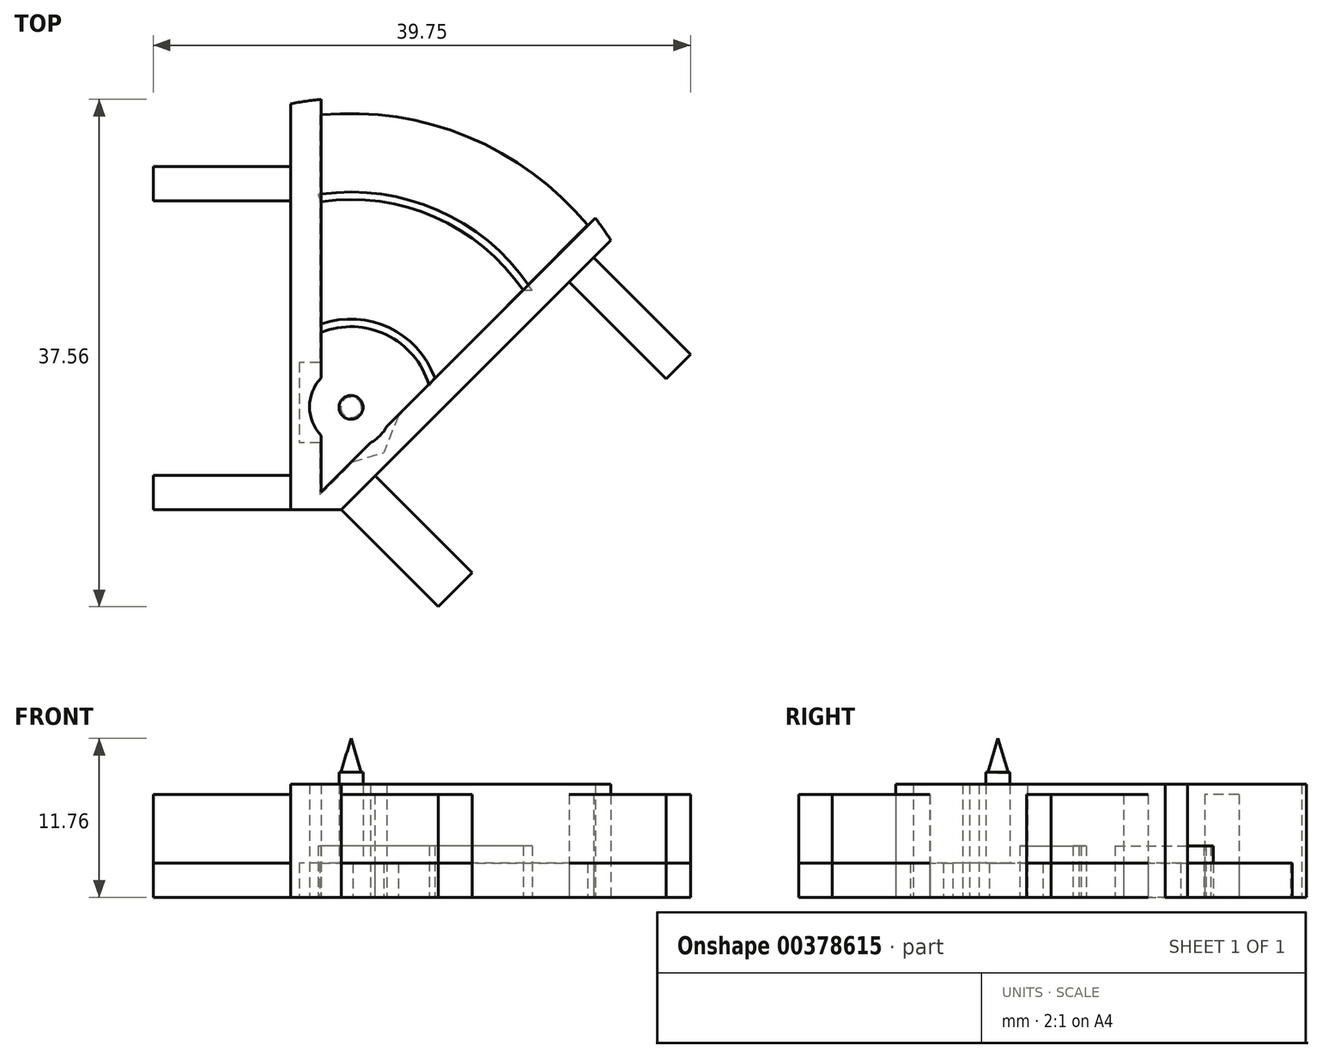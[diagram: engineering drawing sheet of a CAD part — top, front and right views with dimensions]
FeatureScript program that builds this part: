
annotation { "Feature Type Name" : "Feature", "Feature Type Description" : "" }
export const myFeature = defineFeature(function(context is Context, id is Id, definition is map)
    precondition{}
    {
        {
            var Q0;
            Q0=qCreatedBy(makeId("Top.planeOp"),FACE);
            var sketch = newSketch(context, id + "F0", { "sketchPlane" : qUnion([Q0])});
            skCircle(sketch, "E0", {"center": v(0, 0) * mm, "radius": 35.56 * mm});
            skLineSegment(sketch, "E1", {"start": v(0, 0) * mm, "end": v(0, 35.56) * mm});
            skLineSegment(sketch, "E2", {"start": v(0, 0) * mm, "end": v(35.56, 0) * mm});
            skPoint(sketch, "E3", {"position": v(4.45, 7.62) * mm});
            skCircle(sketch, "E4", {"center": v(4.45, 7.62) * mm, "radius": 1.27 * mm});
            skLineSegment(sketch, "E5", {"start": v(2.28, 35.49) * mm, "end": v(2.28, 0) * mm});
            skArc(sketch, "E6", {"start": v(26, 0) * mm, "mid": v(21.73, 22.58) * mm, "end": v(0, 30.04) * mm});
            skLineSegment(sketch, "E7", {"start": v(2.28, 1.31) * mm, "end": v(25.62, 24.66) * mm});
            skLineSegment(sketch, "E8", {"start": v(2.28, -1.47) * mm, "end": v(26.95, 23.2) * mm});
            skArc(sketch, "E9", {"start": v(29.85, 0) * mm, "mid": v(24.32, 25.19) * mm, "end": v(0, 33.77) * mm});
            skCircle(sketch, "E10", {"center": v(4.45, 7.62) * mm, "radius": 3.05 * mm});
            skSolve(sketch);
        }
        {
            var Q0;
            {var subQ0=sQuery(id+"F0.wireOp",EDGE,"E7");var subQ1=sQuery(id+"F0.wireOp",EDGE,"E5");var subQ2=makeQuery(id+"F0.imprint","INTERSECT",VERTEX,{"derivedFrom":[subQ1,subQ0]});Q0=makeQuery(id+"F0.imprint","IMPRINT",FACE,{"disambiguationData":[TD([[makeQuery(id+"F0.imprint","IMPRINT",EDGE,{"disambiguationData":[TD([[subQ2,-1.0]])],"derivedFrom":subQ1}),1.0]])]});}
            var Q1;
            {var subQ5=sQuery(id+"F0.wireOp",EDGE,"E2");var subQ6=sQuery(id+"F0.wireOp",EDGE,"E1");var subQ7=makeQuery(id+"F0.imprint","INTERSECT",VERTEX,{"derivedFrom":[subQ6,subQ5]});Q1=makeQuery(id+"F0.imprint","IMPRINT",FACE,{"disambiguationData":[TD([[makeQuery(id+"F0.imprint","IMPRINT",EDGE,{"disambiguationData":[TD([[subQ7,-1.0]])],"derivedFrom":subQ6}),-1.0]])]});}
            extrude(context, id + "F1", {"entities" : qUnion([Q0, Q1]), "depth" : 8.38 * mm});
        }
        {
            var Q0;
            Q0=qCreatedBy(makeId("Top.planeOp"),FACE);
            var sketch = newSketch(context, id + "F2", { "sketchPlane" : qUnion([Q0])});
            skLineSegment(sketch, "E11", {"start": v(0, 0) * mm, "end": v(3.74, 0) * mm});
            skLineSegment(sketch, "E12", {"start": v(3.74, 0) * mm, "end": v(25.98, 22.24) * mm});
            skLineSegment(sketch, "E13", {"start": v(0, 30.67) * mm, "end": v(0, 0) * mm});
            skLineSegment(sketch, "E14.bottom", {"start": v(0, 2.54) * mm, "end": v(-10.16, 2.54) * mm});
            skLineSegment(sketch, "E14.top", {"start": v(0, 0) * mm, "end": v(-10.16, 0) * mm});
            skLineSegment(sketch, "E14.left", {"start": v(0, 2.54) * mm, "end": v(0, 0) * mm});
            skLineSegment(sketch, "E14.right", {"start": v(-10.16, 2.54) * mm, "end": v(-10.16, 0) * mm});
            skLineSegment(sketch, "E15.bottom", {"start": v(0, 25.4) * mm, "end": v(-10.16, 25.4) * mm});
            skLineSegment(sketch, "E15.top", {"start": v(0, 22.86) * mm, "end": v(-10.16, 22.86) * mm});
            skLineSegment(sketch, "E15.left", {"start": v(0, 25.4) * mm, "end": v(0, 22.86) * mm});
            skLineSegment(sketch, "E15.right", {"start": v(-10.16, 25.4) * mm, "end": v(-10.16, 22.86) * mm});
            skLineSegment(sketch, "E16", {"start": v(3.74, 0) * mm, "end": v(10.93, -7.18) * mm});
            skLineSegment(sketch, "E17", {"start": v(10.93, -7.18) * mm, "end": v(13.43, -4.68) * mm});
            skLineSegment(sketch, "E18", {"start": v(13.43, -4.68) * mm, "end": v(6.24, 2.5) * mm});
            skLineSegment(sketch, "E19", {"start": v(20.61, 16.87) * mm, "end": v(27.8, 9.69) * mm});
            skLineSegment(sketch, "E20", {"start": v(27.8, 9.69) * mm, "end": v(29.6, 11.48) * mm});
            skLineSegment(sketch, "E21", {"start": v(29.6, 11.48) * mm, "end": v(22.4, 18.67) * mm});
            skLineSegment(sketch, "E22", {"start": v(22.4, 18.67) * mm, "end": v(20.61, 16.87) * mm});
            skLineSegment(sketch, "E23", {"start": v(6.24, 2.5) * mm, "end": v(3.74, 0) * mm});
            skLineSegment(sketch, "E24.bottom", {"start": v(-1.4, 25.4) * mm, "end": v(1.32, 25.4) * mm});
            skLineSegment(sketch, "E24.top", {"start": v(-1.4, 22.86) * mm, "end": v(1.32, 22.86) * mm});
            skLineSegment(sketch, "E24.left", {"start": v(-1.4, 25.4) * mm, "end": v(-1.4, 22.86) * mm});
            skLineSegment(sketch, "E24.right", {"start": v(1.32, 25.4) * mm, "end": v(1.32, 22.86) * mm});
            skLineSegment(sketch, "E25.bottom", {"start": v(-2.1, 2.54) * mm, "end": v(1.62, 2.54) * mm});
            skLineSegment(sketch, "E25.top", {"start": v(-2.1, -1.9) * mm, "end": v(1.62, -1.9) * mm});
            skLineSegment(sketch, "E25.left", {"start": v(-2.1, 2.54) * mm, "end": v(-2.1, -1.9) * mm});
            skLineSegment(sketch, "E25.right", {"start": v(1.62, 2.54) * mm, "end": v(1.62, -1.9) * mm});
            skArc(sketch, "E26", {"start": v(21.97, 21.08) * mm, "mid": v(13.1, 27.62) * mm, "end": v(2.18, 29.22) * mm});
            skPoint(sketch, "E27.endSnap0", {"position": v(1.62, 0.32) * mm});
            skLineSegment(sketch, "E28", {"start": v(2.18, 29.22) * mm, "end": v(2.18, 1.1) * mm});
            skLineSegment(sketch, "E29", {"start": v(2.18, 1.1) * mm, "end": v(21.97, 21.08) * mm});
            skLineSegment(sketch, "E30.bottom", {"start": v(2.18, 10.9) * mm, "end": v(0.65, 10.9) * mm});
            skLineSegment(sketch, "E30.top", {"start": v(2.18, 4.95) * mm, "end": v(0.65, 4.95) * mm});
            skLineSegment(sketch, "E30.left", {"start": v(2.18, 10.9) * mm, "end": v(2.18, 4.95) * mm});
            skLineSegment(sketch, "E30.right", {"start": v(0.65, 10.9) * mm, "end": v(0.65, 4.95) * mm});
            skLineSegment(sketch, "E31", {"start": v(7.96, 6.93) * mm, "end": v(6.9, 4.22) * mm});
            skLineSegment(sketch, "E32", {"start": v(4.6, 3.54) * mm, "end": v(6.9, 4.22) * mm});
            skSolve(sketch);
        }
        {
            var Q0;
            Q0=makeQuery(id+"F2.imprint","IMPRINT",FACE,{"disambiguationData":[TD([[makeQuery(id+"F2.imprint","IMPRINT",EDGE,{"derivedFrom":sQuery(id+"F2.wireOp",EDGE,"E16")}),1.0]])]});
            var Q1;
            Q1=makeQuery(id+"F2.imprint","IMPRINT",FACE,{"disambiguationData":[TD([[makeQuery(id+"F2.imprint","IMPRINT",EDGE,{"derivedFrom":sQuery(id+"F2.wireOp",EDGE,"E19")}),1.0]])]});
            var Q2;
            {var subQ0=sQuery(id+"F2.wireOp",EDGE,"E14.bottom");Q2=makeQuery(id+"F2.imprint","IMPRINT",FACE,{"disambiguationData":[TD([[makeQuery(id+"F2.imprint","IMPRINT",EDGE,{"derivedFrom":subQ0}),1.0]])]});}
            var Q3;
            Q3=makeQuery(id+"F2.imprint","IMPRINT",FACE,{"disambiguationData":[TD([[makeQuery(id+"F2.imprint","IMPRINT",EDGE,{"derivedFrom":sQuery(id+"F2.wireOp",EDGE,"E15.bottom")}),1.0]])]});
            var Q4;
            {var subQ0=sQuery(id+"F2.wireOp",EDGE,"E15.left");Q4=makeQuery(id+"F2.imprint","IMPRINT",FACE,{"disambiguationData":[TD([[makeQuery(id+"F2.imprint","IMPRINT",EDGE,{"derivedFrom":subQ0}),1.0]])]});}
            var Q5;
            {var subQ0=sQuery(id+"F2.wireOp",EDGE,"E31");Q5=makeQuery(id+"F2.imprint","IMPRINT",FACE,{"disambiguationData":[TD([[makeQuery(id+"F2.imprint","IMPRINT",EDGE,{"derivedFrom":subQ0}),-1.0]])]});}
            var Q6;
            Q6=makeQuery(id+"F2.imprint","IMPRINT",FACE,{"disambiguationData":[TD([[makeQuery(id+"F2.imprint","IMPRINT",EDGE,{"derivedFrom":sQuery(id+"F2.wireOp",EDGE,"E30.bottom")}),1.0]])]});
            var Q7;
            {var subQ0=sQuery(id+"F2.wireOp",EDGE,"E14.left");Q7=makeQuery(id+"F2.imprint","IMPRINT",FACE,{"disambiguationData":[TD([[makeQuery(id+"F2.imprint","IMPRINT",EDGE,{"derivedFrom":subQ0}),1.0]])]});}
            var Q8;
            {var subQ0=sQuery(id+"F2.wireOp",EDGE,"E15.left");Q8=makeQuery(id+"F2.imprint","IMPRINT",FACE,{"disambiguationData":[TD([[makeQuery(id+"F2.imprint","IMPRINT",EDGE,{"derivedFrom":subQ0}),-1.0]])]});}
            var Q9;
            {var subQ5=sQuery(id+"F2.wireOp",EDGE,"E26");Q9=makeQuery(id+"F2.imprint","IMPRINT",FACE,{"disambiguationData":[TD([[makeQuery(id+"F2.imprint","IMPRINT",EDGE,{"derivedFrom":subQ5}),1.0]])]});}
            var Q10;
            {var subQ0=sQuery(id+"F2.wireOp",EDGE,"E14.left");Q10=makeQuery(id+"F2.imprint","IMPRINT",FACE,{"disambiguationData":[TD([[makeQuery(id+"F2.imprint","IMPRINT",EDGE,{"derivedFrom":subQ0}),-1.0]])]});}
            extrude(context, id + "F3", {"entities" : qUnion([Q0, Q1, Q2, Q3, Q4, Q5, Q6, Q7, Q8, Q9, Q10]), "depth" : 2.54 * mm});
        }
        {
            var Q0;
            Q0=qCreatedBy(makeId("Top.planeOp"),FACE);
            var sketch = newSketch(context, id + "F4", { "sketchPlane" : qUnion([Q0])});
            skPoint(sketch, "E33", {"position": v(4.47, 7.58) * mm});
            skCircle(sketch, "E34", {"center": v(4.47, 7.58) * mm, "radius": 0.89 * mm});
            skSolve(sketch);
        }
        {
            var Q0;
            Q0 = qSketchRegion(id + "F4", true);
            extrude(context, id + "F5", {"entities" : qUnion([Q0]), "operationType" : NewBodyOperationType.ADD, "depth" : 9.25 * mm, "hasSecondDirection" : true, "secondDirectionOppositeDirection" : false, "secondDirectionDepth" : 0 * mm});
        }
        {
            var Q0;
            Q0=qCreatedBy(makeId("Top.planeOp"),FACE);
            var sketch = newSketch(context, id + "F6", { "sketchPlane" : qUnion([Q0])});
            skArc(sketch, "E35", {"start": v(10.66, 9.76) * mm, "mid": v(7.26, 13.5) * mm, "end": v(2.22, 13.71) * mm});
            skArc(sketch, "E36", {"start": v(10.25, 9.17) * mm, "mid": v(7.12, 12.94) * mm, "end": v(2.22, 13.1) * mm});
            skArc(sketch, "E37", {"start": v(17.2, 16.24) * mm, "mid": v(10.65, 21.67) * mm, "end": v(2.22, 22.8) * mm});
            skArc(sketch, "E38", {"start": v(17.87, 16.24) * mm, "mid": v(11, 22.12) * mm, "end": v(2.04, 23.32) * mm});
            skLineSegment(sketch, "E39", {"start": v(2.04, 23.32) * mm, "end": v(2.22, 22.8) * mm});
            skLineSegment(sketch, "E40", {"start": v(17.87, 16.24) * mm, "end": v(17.2, 16.24) * mm});
            skLineSegment(sketch, "E41", {"start": v(10.66, 9.76) * mm, "end": v(10.25, 9.17) * mm});
            skLineSegment(sketch, "E42", {"start": v(2.22, 13.71) * mm, "end": v(2.22, 13.1) * mm});
            skLineSegment(sketch, "E43", {"start": v(10.25, 9.17) * mm, "end": v(10.66, 9.76) * mm});
            skSolve(sketch);
        }
        {
            var Q0;
            Q0 = qSketchRegion(id + "F6", true);
            extrude(context, id + "F7", {"entities" : qUnion([Q0]), "depth" : 3.8 * mm});
        }
        {
            var Q0;
            Q0=qCreatedBy(makeId("Front.planeOp"),FACE);
            cPlane(context, id + "F8", {"entities" : qUnion([Q0]), "cplaneType" : CPlaneType.OFFSET, "offset" : 7.57 * mm, "oppositeDirection" : true, "width" : 152.4 * mm, "height" : 152.4 * mm});
        }
        {
            var Q0;
            Q0=qCreatedBy(id+"F8.planeOp",FACE);
            var sketch = newSketch(context, id + "F9", { "sketchPlane" : qUnion([Q0])});
            skLineSegment(sketch, "E44", {"start": v(4.47, 10.2) * mm, "end": v(4.47, 8.38) * mm});
            skLineSegment(sketch, "E45", {"start": v(4.47, 8.38) * mm, "end": v(4.47, 0) * mm});
            skLineSegment(sketch, "E46", {"start": v(4.47, 9.18) * mm, "end": v(4.47, 11.76) * mm});
            skLineSegment(sketch, "E47", {"start": v(4.47, 11.76) * mm, "end": v(5.24, 9.18) * mm});
            skLineSegment(sketch, "E48", {"start": v(5.24, 9.18) * mm, "end": v(4.47, 9.18) * mm});
            skSolve(sketch);
        }
        {
            var Q0;
            Q0 = qSketchRegion(id + "F9", true);
            var Q1;
            Q1=sQuery(id+"F9.wireOp",EDGE,"E45");
            revolve(context, id + "F10", {"entities" : qUnion([Q0]), "axis" : qUnion([Q1]), "revolveType" : RevolveType.FULL});
        }
        {
            var Q0;
            Q0=makeQuery(id+"F2.imprint","IMPRINT",FACE,{"disambiguationData":[TD([[makeQuery(id+"F2.imprint","IMPRINT",EDGE,{"derivedFrom":sQuery(id+"F2.wireOp",EDGE,"E15.bottom")}),1.0]])]});
            var Q1;
            {var subQ0=sQuery(id+"F2.wireOp",EDGE,"E14.bottom");Q1=makeQuery(id+"F2.imprint","IMPRINT",FACE,{"disambiguationData":[TD([[makeQuery(id+"F2.imprint","IMPRINT",EDGE,{"derivedFrom":subQ0}),1.0]])]});}
            var Q2;
            {var subQ0=sQuery(id+"F2.wireOp",EDGE,"E14.left");Q2=makeQuery(id+"F2.imprint","IMPRINT",FACE,{"disambiguationData":[TD([[makeQuery(id+"F2.imprint","IMPRINT",EDGE,{"derivedFrom":subQ0}),-1.0]])]});}
            var Q3;
            {var subQ0=sQuery(id+"F2.wireOp",EDGE,"E15.left");Q3=makeQuery(id+"F2.imprint","IMPRINT",FACE,{"disambiguationData":[TD([[makeQuery(id+"F2.imprint","IMPRINT",EDGE,{"derivedFrom":subQ0}),-1.0]])]});}
            var Q4;
            Q4=makeQuery(id+"F2.imprint","IMPRINT",FACE,{"disambiguationData":[TD([[makeQuery(id+"F2.imprint","IMPRINT",EDGE,{"derivedFrom":sQuery(id+"F2.wireOp",EDGE,"E16")}),1.0]])]});
            var Q5;
            Q5=makeQuery(id+"F2.imprint","IMPRINT",FACE,{"disambiguationData":[TD([[makeQuery(id+"F2.imprint","IMPRINT",EDGE,{"derivedFrom":sQuery(id+"F2.wireOp",EDGE,"E19")}),1.0]])]});
            extrude(context, id + "F11", {"entities" : qUnion([Q0, Q1, Q2, Q3, Q4, Q5]), "depth" : 7.62 * mm});
        }
    });
